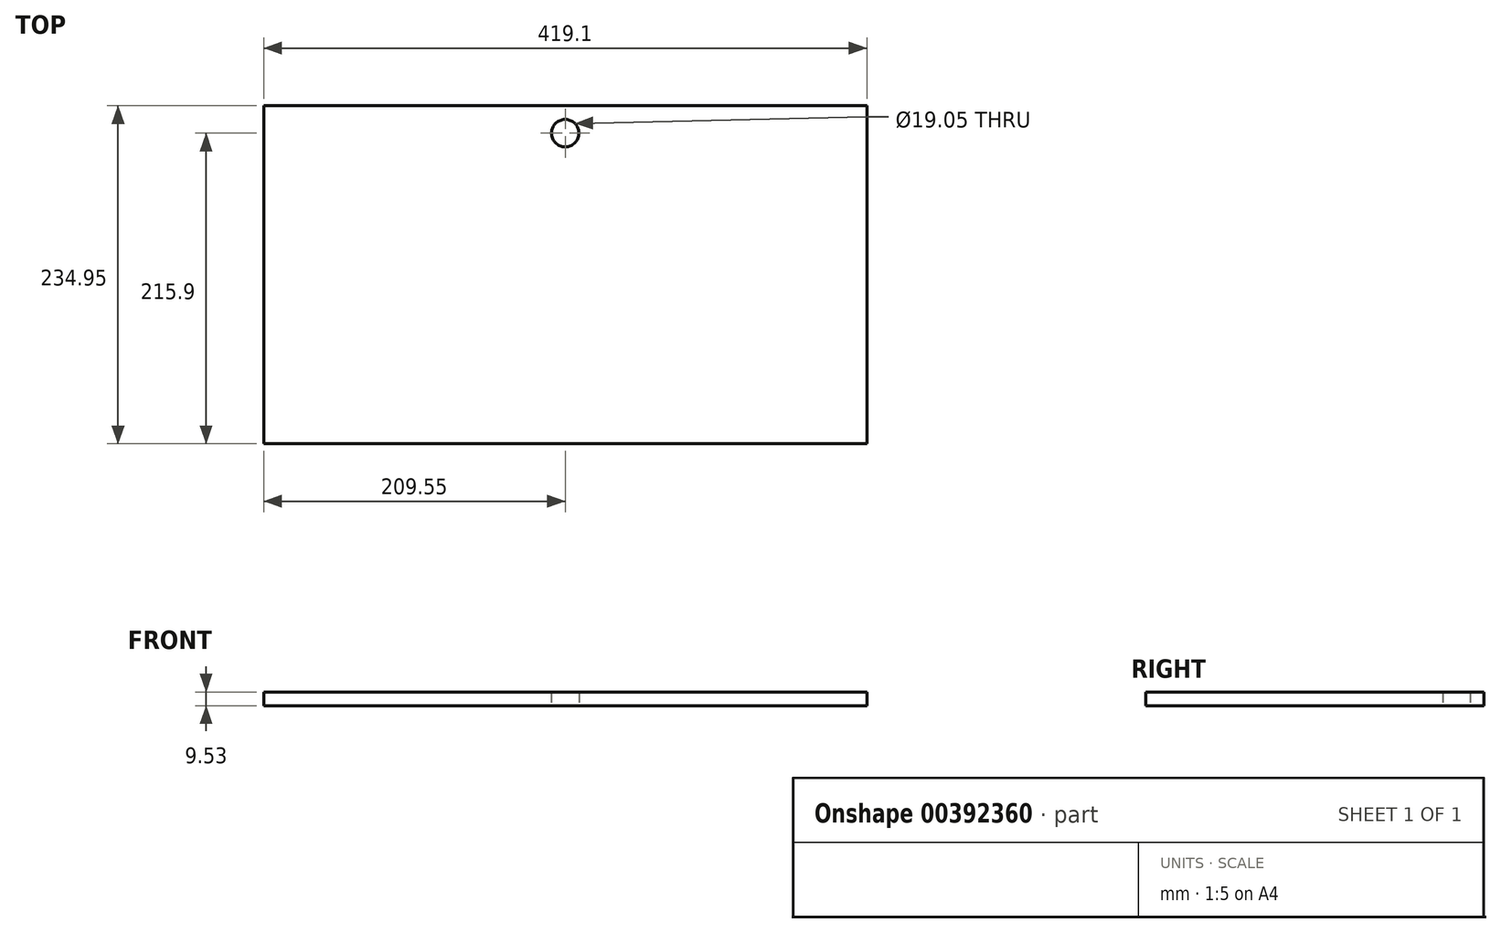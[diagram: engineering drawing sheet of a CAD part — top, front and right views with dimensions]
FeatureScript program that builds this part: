
annotation { "Feature Type Name" : "Feature", "Feature Type Description" : "" }
export const myFeature = defineFeature(function(context is Context, id is Id, definition is map)
    precondition{}
    {
        {
            var Q0;
            Q0=qCreatedBy(makeId("Top.planeOp"),FACE);
            var sketch = newSketch(context, id + "F0", { "sketchPlane" : qUnion([Q0])});
            skLineSegment(sketch, "E0.bottom", {"start": v(-209.55, 0) * mm, "end": v(209.55, 0) * mm});
            skLineSegment(sketch, "E0.top", {"start": v(-209.55, -234.95) * mm, "end": v(209.55, -234.95) * mm});
            skLineSegment(sketch, "E0.left", {"start": v(-209.55, 0) * mm, "end": v(-209.55, -234.95) * mm});
            skLineSegment(sketch, "E0.right", {"start": v(209.55, 0) * mm, "end": v(209.55, -234.95) * mm});
            skCircle(sketch, "E1", {"center": v(0, -19.05) * mm, "radius": 9.53 * mm});
            skSolve(sketch);
        }
        {
            var Q0;
            Q0=makeQuery(id+"F0.imprint","IMPRINT",FACE,{"disambiguationData":[TD([[makeQuery(id+"F0.imprint","IMPRINT",EDGE,{"derivedFrom":sQuery(id+"F0.wireOp",EDGE,"E0.bottom")}),-1.0]])]});
            extrude(context, id + "F1", {"entities" : qUnion([Q0]), "depth" : 9.52 * mm});
        }
    });
